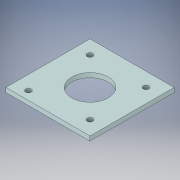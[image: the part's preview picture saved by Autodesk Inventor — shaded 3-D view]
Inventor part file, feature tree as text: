
AUTODESK INVENTOR PART (.ipt)
format: ipt  version: 2019 (Build 230136000, 136)  size: 136,704 bytes
history: native  units: mm
features: other x1, extrude x1, sketch x1
ambient origin geometry x8: Origin, YZ Plane, XZ Plane, XY Plane, X Axis, Y Axis, Z Axis, Center Point
bodies: Body1 (feature_tree)
feature tree (3):
  other  "Sólido1"
  extrude  "Extrusión1"  Depth=3.18mm TaperAngle=0.0deg
  sketch  "Boceto1"  dims[d0=26.0mm d1=60.0mm d2=60.0mm d3=4.0mm d4=4.0mm d5=4.0mm d6=4.0mm d7=40.0mm d8=20.0mm d9=20.0mm d10=40.0mm d11=40.0mm d12=20.0mm d13=40.0mm d14=20.0mm d15=3.18mm d16=0.0mm]
